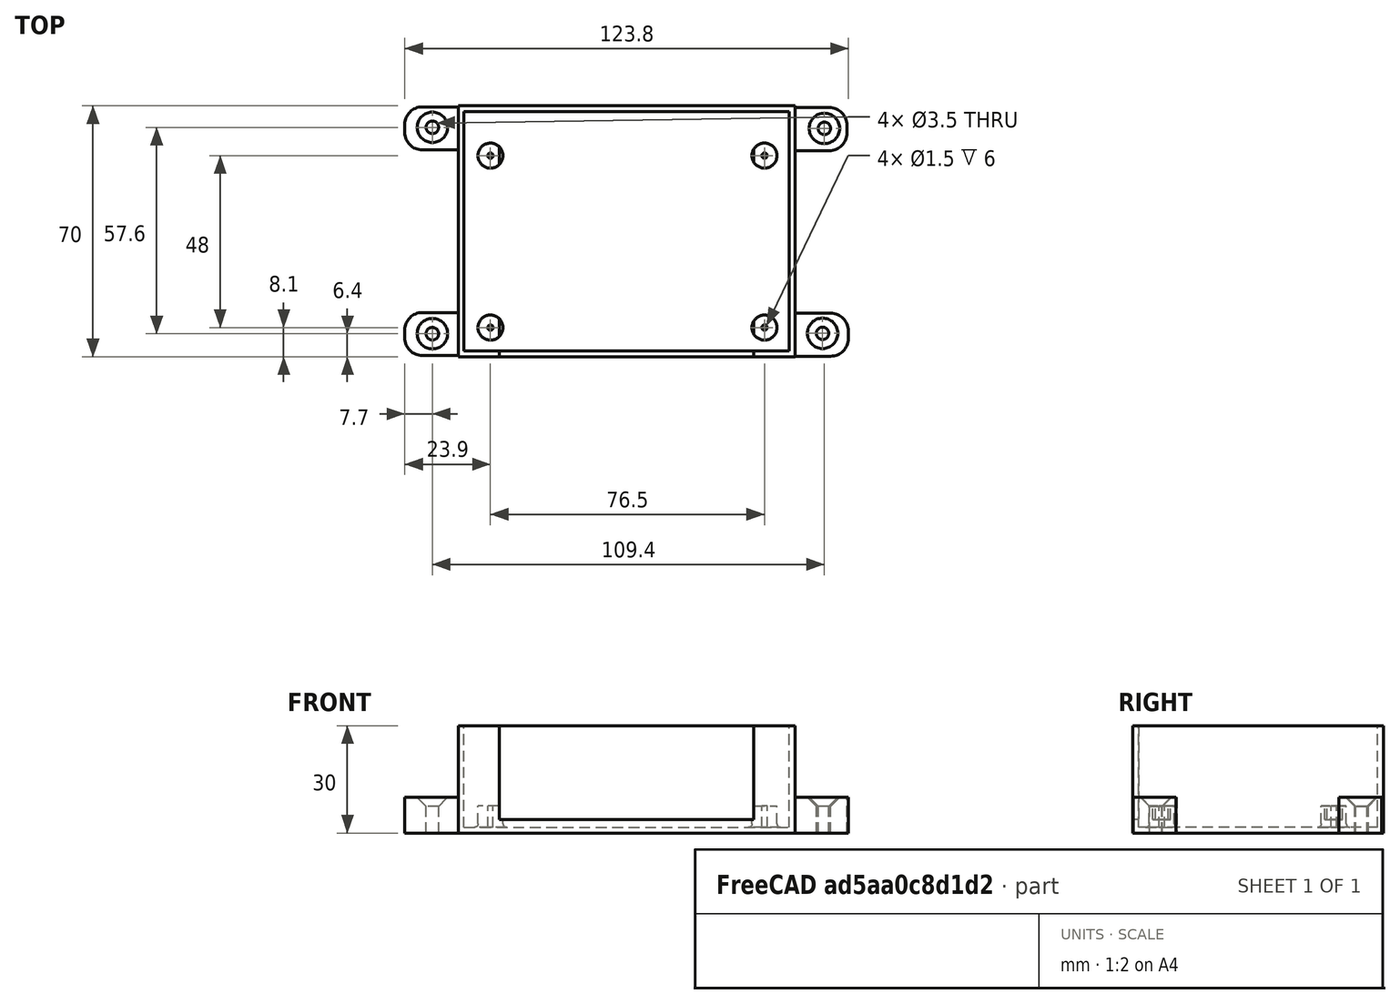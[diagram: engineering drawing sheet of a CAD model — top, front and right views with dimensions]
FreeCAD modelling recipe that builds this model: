
FCSTD DOCUMENT  (FreeCAD 0.19R22846 (Git))
Label: rainsensorhousing_2
License: All rights reserved
LicenseURL: http://en.wikipedia.org/wiki/All_rights_reserved
objects: Part::Cylinder×16, Part::Box×7, Part::MultiFuse×7, Part::Cut×7, Part::Fillet×4, Part::Thickness×1, Part::Refine×1, Part::Chamfer×1
note: 44 computed .brp shape members not serialized (recipe doc carries the construction recipe); baked Part::Feature solids carry a one-line shape summary decoded from their .brp

FEATURE [Part::Box] Box  label="Würfel"
  AttacherType = Attacher::AttachEngine3D
  Height = 1.5
  Length = 86
  Width = 58
FEATURE [Part::Cylinder] Cylinder  label="Zylinder"
  Angle = 360
  AttacherType = Attacher::AttachEngine3D
  Height = 10
  Placement = pos=(5,5,0) rot=(0,0,1;0rad)
  Radius = 1.5
FEATURE [Part::Cylinder] Cylinder001  label="Zylinder001"
  Angle = 360
  AttacherType = Attacher::AttachEngine3D
  Height = 10
  Placement = pos=(5,53,0) rot=(0,0,1;0rad)
  Radius = 1.5
FEATURE [Part::Cylinder] Cylinder002  label="Zylinder002"
  Angle = 360
  AttacherType = Attacher::AttachEngine3D
  Height = 10
  Placement = pos=(81.5,5,0) rot=(0,0,1;0rad)
  Radius = 1.5
FEATURE [Part::Cylinder] Cylinder003  label="Zylinder003"
  Angle = 360
  AttacherType = Attacher::AttachEngine3D
  Height = 10
  Placement = pos=(81.5,53,0) rot=(0,0,1;0rad)
  Radius = 1.5
FEATURE [Part::MultiFuse] Fusion
  Shapes = -> [Cylinder,Cylinder001,Cylinder002,Cylinder003]
FEATURE [Part::Cut] Cut
  Base = -> Box
  Tool = -> Fusion
FEATURE [Part::Box] Box001  label="Würfel001"
  AttacherType = Attacher::AttachEngine3D
  Height = 30
  Length = 71
  Placement = pos=(7.49857,58.9,26) rot=(1,0,0;3.14159rad)
  Width = 67
FEATURE [Part::MultiFuse] Fusion001
  Placement = pos=(0,-5,2.8) rot=(0,0,1;0rad)
  Shapes = -> [Cut,Box001]
FEATURE [Part::Box] Box002  label="Würfel002"
  AttacherType = Attacher::AttachEngine3D
  Height = 30
  Length = 94
  Placement = pos=(-4.00143,-8.1,-5) rot=(0,0,1;0rad)
  Width = 70
FEATURE [Part::Thickness] Thickness
  Faces = -> Box002 [Face6]
  Intersection = false
  Join = 0
  Mode = 0
  SelfIntersection = false
  Value = -1.6
FEATURE [Part::Cylinder] Cylinder004  label="Zylinder004"
  Angle = 360
  AttacherType = Attacher::AttachEngine3D
  Height = 6
  Placement = pos=(5,0,-3.4) rot=(0,0,1;0rad)
  Radius = 3.5
FEATURE [Part::Cylinder] Cylinder005  label="Zylinder005"
  Angle = 360
  AttacherType = Attacher::AttachEngine3D
  Height = 10
  Placement = pos=(5,0,-6) rot=(0,0,1;0rad)
  Radius = 0.75
FEATURE [Part::Cut] Cut001
  Base = -> Cylinder004
  Tool = -> Cylinder005
FEATURE [Part::Cylinder] Cylinder006  label="Zylinder006"
  Angle = 360
  AttacherType = Attacher::AttachEngine3D
  Height = 6
  Placement = pos=(5,0,-3.4) rot=(0,0,1;0rad)
  Radius = 3.5
FEATURE [Part::Cylinder] Cylinder007  label="Zylinder007"
  Angle = 360
  AttacherType = Attacher::AttachEngine3D
  Height = 10
  Placement = pos=(5,0,-6) rot=(0,0,1;0rad)
  Radius = 0.75
FEATURE [Part::Cut] Cut002
  Base = -> Cylinder006
  Placement = pos=(0,48,0) rot=(0,0,1;0rad)
  Tool = -> Cylinder007
FEATURE [Part::Cylinder] Cylinder008  label="Zylinder008"
  Angle = 360
  AttacherType = Attacher::AttachEngine3D
  Height = 6
  Placement = pos=(5,0,-3.4) rot=(0,0,1;0rad)
  Radius = 3.5
FEATURE [Part::Cylinder] Cylinder009  label="Zylinder009"
  Angle = 360
  AttacherType = Attacher::AttachEngine3D
  Height = 10
  Placement = pos=(5,0,-6) rot=(0,0,1;0rad)
  Radius = 0.75
FEATURE [Part::Cut] Cut003
  Base = -> Cylinder008
  Placement = pos=(76.5,48,0) rot=(0,0,1;0rad)
  Tool = -> Cylinder009
FEATURE [Part::Cylinder] Cylinder010  label="Zylinder010"
  Angle = 360
  AttacherType = Attacher::AttachEngine3D
  Height = 10
  Placement = pos=(5,0,-6) rot=(0,0,1;0rad)
  Radius = 0.75
FEATURE [Part::Cylinder] Cylinder011  label="Zylinder011"
  Angle = 360
  AttacherType = Attacher::AttachEngine3D
  Height = 6
  Placement = pos=(5,0,-3.4) rot=(0,0,1;0rad)
  Radius = 3.5
FEATURE [Part::Cut] Cut004
  Base = -> Cylinder011
  Placement = pos=(76.5,-7.1e-15,0) rot=(0,0,1;0rad)
  Tool = -> Cylinder010
FEATURE [Part::MultiFuse] Fusion002
  Shapes = -> [Cut004,Cut001,Cut002,Cut003]
FEATURE [Part::MultiFuse] Fusion003
  Shapes = -> [Fusion002,Thickness]
FEATURE [Part::Fillet] Fillet
  Base = -> Fusion003
  Edges = 2 edges r=1: [Edge27,Edge28]
FEATURE [Part::Fillet] Fillet001
  Base = -> Fillet
  Edges = 2 edges r=1: [Edge6,Edge7]
FEATURE [Part::Box] Box003  label="Würfel003"
  AttacherType = Attacher::AttachEngine3D
  Height = 10
  Length = 15
  Placement = pos=(-18.9,-7.8,-5) rot=(0,0,1;0rad)
  Width = 12
FEATURE [Part::Cylinder] Cylinder012  label="Zylinder012"
  Angle = 360
  AttacherType = Attacher::AttachEngine3D
  Height = 20
  Placement = pos=(-11.2,-1.7,-5) rot=(0,0,1;0rad)
  Radius = 1.75
FEATURE [Part::Box] Box004  label="Würfel004"
  AttacherType = Attacher::AttachEngine3D
  Height = 10
  Length = 15
  Placement = pos=(-18.9,49.6,-5) rot=(0,0,1;0rad)
  Width = 12
FEATURE [Part::Box] Box005  label="Würfel005"
  AttacherType = Attacher::AttachEngine3D
  Height = 10
  Length = 15
  Placement = pos=(89.9,-8,-5) rot=(0,0,1;0rad)
  Width = 12
FEATURE [Part::Box] Box006  label="Würfel006"
  AttacherType = Attacher::AttachEngine3D
  Height = 10
  Length = 15
  Placement = pos=(89.5,49.4,-5) rot=(0,0,1;0rad)
  Width = 12
FEATURE [Part::Cylinder] Cylinder013  label="Zylinder013"
  Angle = 360
  AttacherType = Attacher::AttachEngine3D
  Height = 20
  Placement = pos=(97.7,-1.6,-5) rot=(0,0,1;0rad)
  Radius = 1.75
FEATURE [Part::Cylinder] Cylinder014  label="Zylinder014"
  Angle = 360
  AttacherType = Attacher::AttachEngine3D
  Height = 20
  Placement = pos=(98.2,55.6,-5) rot=(0,0,1;0rad)
  Radius = 1.75
FEATURE [Part::Cylinder] Cylinder015  label="Zylinder015"
  Angle = 360
  AttacherType = Attacher::AttachEngine3D
  Height = 20
  Placement = pos=(-11.2,55.9,-5) rot=(0,0,1;0rad)
  Radius = 1.75
FEATURE [Part::MultiFuse] Fusion004
  Shapes = -> [Cylinder012,Cylinder014,Cylinder013,Cylinder015]
FEATURE [Part::MultiFuse] Fusion005
  Shapes = -> [Box003,Box004,Box005,Box006]
FEATURE [Part::Cut] Cut005
  Base = -> Fusion005
  Tool = -> Fusion004
FEATURE [Part::MultiFuse] Fusion006
  Shapes = -> [Cut005,Fillet001]
FEATURE [Part::Refine] Fusion006001
  Source = -> Fusion006
FEATURE [Part::Fillet] Fillet002
  Base = -> Fusion006001
  Edges = 4 edges r=4.9: [Edge1,Edge3,Edge35,Edge40]
FEATURE [Part::Fillet] Fillet003
  Base = -> Fillet002
  Edges = 4 edges r=4.9: [Edge68,Edge72,Edge74,Edge76]
FEATURE [Part::Chamfer] Chamfer
  Base = -> Fillet003
  Edges = 4 edges r=2.5: [Edge89,Edge91,Edge93,Edge95]
FEATURE [Part::Cut] Cut006
  Base = -> Chamfer
  Tool = -> Fusion001
